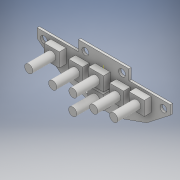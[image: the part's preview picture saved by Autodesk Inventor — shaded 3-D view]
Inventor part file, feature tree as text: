
AUTODESK INVENTOR PART (.ipt)
format: ipt  version: 2017 (Build 210142000, 142)  size: 174,592 bytes
history: native  units: mm
features: extrude x3, sketch x1, plane x1
ambient origin geometry x8: Origin, YZ Plane, XZ Plane, XY Plane, X Axis, Y Axis, Z Axis, Center Point
bodies: Solid1 (feature_tree)
feature tree (5):
  sketch  "Sketch1"  dims[d1=1.0mm d2=0.0mm d3=3.0mm d4=0.0mm d5=13.0mm d6=0.0mm d7=-29.0mm]
  extrude  "Extrusion1"  Depth=3.0mm TaperAngle=0.0deg
  extrude  "Extrusion2"  Depth=13.0mm TaperAngle=0.0deg
  extrude  "Extrusion3"  [1 undecoded]
  plane  "Work Plane1"
note: 1 required parameter value undecoded (feature->parameter linkage not recoverable at this tier; creation-order binding heuristic only, values carry confidence <= 0.55)
